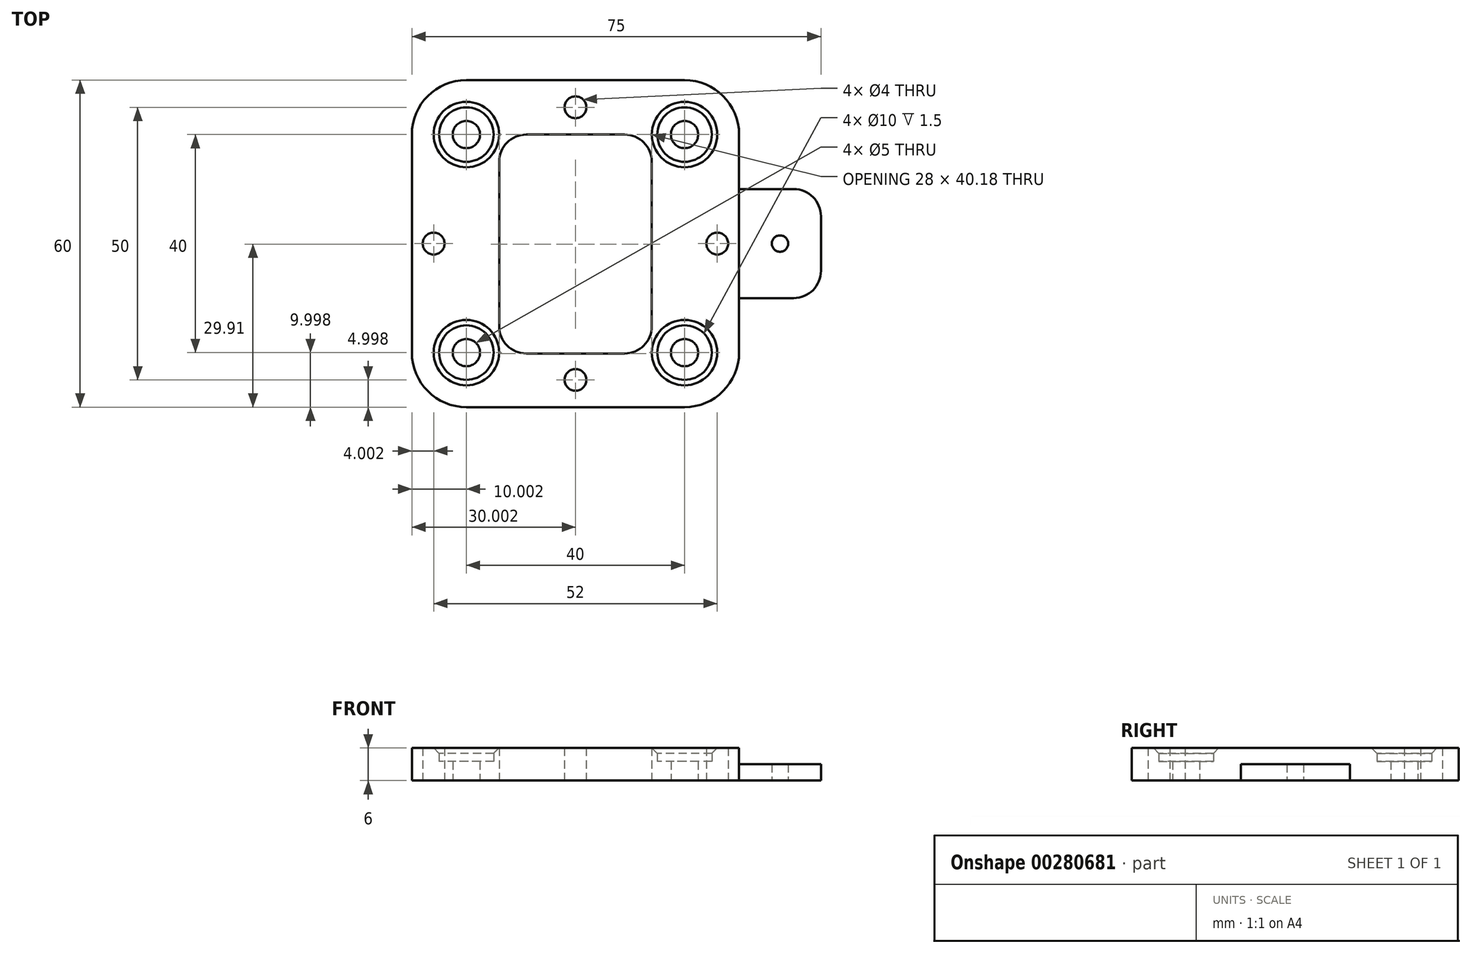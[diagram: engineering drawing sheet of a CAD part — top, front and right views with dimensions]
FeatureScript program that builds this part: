
annotation { "Feature Type Name" : "Feature", "Feature Type Description" : "" }
export const myFeature = defineFeature(function(context is Context, id is Id, definition is map)
    precondition{}
    {
        {
            var Q0;
            Q0=qCreatedBy(makeId("Top.planeOp"),FACE);
            var sketch = newSketch(context, id + "F0", { "sketchPlane" : qUnion([Q0])});
            skLineSegment(sketch, "E0.bottom", {"start": v(-88.55, 39.85) * mm, "end": v(-28.55, 39.85) * mm});
            skLineSegment(sketch, "E0.top", {"start": v(-88.55, -20.15) * mm, "end": v(-28.55, -20.15) * mm});
            skLineSegment(sketch, "E0.left", {"start": v(-88.55, 39.85) * mm, "end": v(-88.55, -20.15) * mm});
            skLineSegment(sketch, "E0.right", {"start": v(-28.55, 39.85) * mm, "end": v(-28.55, -20.15) * mm});
            skLineSegment(sketch, "E1.0", {"start": v(-78.55, 29.85) * mm, "end": v(-38.55, 29.85) * mm, "construction": true});
            skLineSegment(sketch, "E1.1", {"start": v(-78.55, 29.85) * mm, "end": v(-78.55, -10.15) * mm, "construction": true});
            skLineSegment(sketch, "E1.2", {"start": v(-78.55, -10.15) * mm, "end": v(-38.55, -10.15) * mm, "construction": true});
            skLineSegment(sketch, "E1.3", {"start": v(-38.55, 29.85) * mm, "end": v(-38.55, -10.15) * mm, "construction": true});
            skCircle(sketch, "E2", {"center": v(-78.55, 29.85) * mm, "radius": 5 * mm});
            skCircle(sketch, "E3", {"center": v(-78.55, -10.15) * mm, "radius": 5 * mm});
            skCircle(sketch, "E4", {"center": v(-38.55, 29.85) * mm, "radius": 5 * mm});
            skCircle(sketch, "E5", {"center": v(-38.55, -10.15) * mm, "radius": 5 * mm});
            skCircle(sketch, "E6", {"center": v(-78.55, 29.85) * mm, "radius": 2.5 * mm});
            skCircle(sketch, "E7", {"center": v(-38.55, 29.85) * mm, "radius": 2.5 * mm});
            skCircle(sketch, "E8", {"center": v(-38.55, -10.15) * mm, "radius": 2.5 * mm});
            skCircle(sketch, "E9", {"center": v(-78.55, -10.15) * mm, "radius": 2.5 * mm});
            skLineSegment(sketch, "E10.0", {"start": v(-72.55, 29.85) * mm, "end": v(-72.55, -10.33) * mm});
            skLineSegment(sketch, "E11.0", {"start": v(-44.55, 29.85) * mm, "end": v(-44.55, -10.33) * mm});
            skLineSegment(sketch, "E12", {"start": v(-72.55, 29.85) * mm, "end": v(-44.55, 29.85) * mm});
            skLineSegment(sketch, "E13", {"start": v(-44.55, -10.33) * mm, "end": v(-72.55, -10.33) * mm});
            skCircle(sketch, "E14", {"center": v(-84.55, 9.85) * mm, "radius": 2 * mm});
            skPoint(sketch, "E14.centerSnap0", {"position": v(-78.55, 9.85) * mm});
            skCircle(sketch, "E15", {"center": v(-32.55, 9.85) * mm, "radius": 2 * mm});
            skPoint(sketch, "E15.centerSnap0", {"position": v(-38.55, 9.85) * mm});
            skLineSegment(sketch, "E16.bottom", {"start": v(-28.55, 19.85) * mm, "end": v(-13.55, 19.85) * mm});
            skLineSegment(sketch, "E16.top", {"start": v(-28.55, -0.15) * mm, "end": v(-13.55, -0.15) * mm});
            skLineSegment(sketch, "E16.left", {"start": v(-28.55, 19.85) * mm, "end": v(-28.55, -0.15) * mm});
            skLineSegment(sketch, "E16.right", {"start": v(-13.55, 19.85) * mm, "end": v(-13.55, -0.15) * mm});
            skPoint(sketch, "E16.middle", {"position": v(-21.05, 9.85) * mm});
            skCircle(sketch, "E17", {"center": v(-21.05, 9.85) * mm, "radius": 1.5 * mm});
            skCircle(sketch, "E18", {"center": v(-58.55, 34.85) * mm, "radius": 2 * mm});
            skPoint(sketch, "E18.centerSnap0", {"position": v(-58.55, 29.85) * mm});
            skCircle(sketch, "E19", {"center": v(-58.55, -15.15) * mm, "radius": 2 * mm});
            skPoint(sketch, "E19.centerSnap0", {"position": v(-58.55, -10.33) * mm});
            skSolve(sketch);
        }
        {
            var Q0;
            Q0=makeQuery(id+"F0.imprint","IMPRINT",FACE,{"disambiguationData":[TD([[makeQuery(id+"F0.imprint","IMPRINT",EDGE,{"derivedFrom":sQuery(id+"F0.wireOp",EDGE,"E0.bottom")}),-1.0]])]});
            extrude(context, id + "F1", {"entities" : qUnion([Q0]), "depth" : 6 * mm, "offsetDistance" : 25 * mm});
        }
        {
            var Q0;
            Q0=makeQuery(id+"F0.imprint","IMPRINT",FACE,{"disambiguationData":[TD([[makeQuery(id+"F0.imprint","IMPRINT",EDGE,{"derivedFrom":sQuery(id+"F0.wireOp",EDGE,"E2")}),1.0]])]});
            var Q1;
            Q1=makeQuery(id+"F0.imprint","IMPRINT",FACE,{"disambiguationData":[TD([[makeQuery(id+"F0.imprint","IMPRINT",EDGE,{"derivedFrom":sQuery(id+"F0.wireOp",EDGE,"E3")}),1.0]])]});
            var Q2;
            Q2=makeQuery(id+"F0.imprint","IMPRINT",FACE,{"disambiguationData":[TD([[makeQuery(id+"F0.imprint","IMPRINT",EDGE,{"derivedFrom":sQuery(id+"F0.wireOp",EDGE,"E4")}),1.0]])]});
            var Q3;
            Q3=makeQuery(id+"F0.imprint","IMPRINT",FACE,{"disambiguationData":[TD([[makeQuery(id+"F0.imprint","IMPRINT",EDGE,{"derivedFrom":sQuery(id+"F0.wireOp",EDGE,"E5")}),1.0]])]});
            extrude(context, id + "F2", {"entities" : qUnion([Q0, Q1, Q2, Q3]), "operationType" : NewBodyOperationType.ADD, "depth" : 3.5 * mm, "offsetDistance" : 25 * mm});
        }
        {
            var Q0;
            Q0=makeQuery(id+"F0.imprint","IMPRINT",FACE,{"disambiguationData":[TD([[makeQuery(id+"F0.imprint","IMPRINT",EDGE,{"derivedFrom":sQuery(id+"F0.wireOp",EDGE,"E16.bottom")}),-1.0]])]});
            extrude(context, id + "F3", {"entities" : qUnion([Q0]), "operationType" : NewBodyOperationType.ADD, "depth" : 3 * mm, "offsetDistance" : 25 * mm});
        }
        {
            var Q0;
            Q0=makeQuery(id+"F1.opExtrude","SWEPT_EDGE",EDGE,{"disambiguationData":[OSD([sQuery(id+"F0.wireOp",EDGE,"E0.bottom"),sQuery(id+"F0.wireOp",EDGE,"E0.left")])]});
            var Q1;
            Q1=makeQuery(id+"F1.opExtrude","SWEPT_EDGE",EDGE,{"disambiguationData":[OSD([sQuery(id+"F0.wireOp",EDGE,"E0.top"),sQuery(id+"F0.wireOp",EDGE,"E0.left")])]});
            var Q2;
            Q2=makeQuery(id+"F1.opExtrude","SWEPT_EDGE",EDGE,{"disambiguationData":[OSD([sQuery(id+"F0.wireOp",EDGE,"E0.top"),sQuery(id+"F0.wireOp",EDGE,"E0.right")])]});
            var Q3;
            Q3=makeQuery(id+"F1.opExtrude","SWEPT_EDGE",EDGE,{"disambiguationData":[OSD([sQuery(id+"F0.wireOp",EDGE,"E0.bottom"),sQuery(id+"F0.wireOp",EDGE,"E0.right")])]});
            fillet(context, id + "F4", {"entities" : qUnion([Q0, Q1, Q2, Q3]), "radius" : 10 * mm, "tangentPropagation" : true, "allowEdgeOverflow" : false});
        }
        {
            var Q0;
            Q0=makeQuery(id+"F1.opExtrude","SWEPT_EDGE",EDGE,{"disambiguationData":[OSD([sQuery(id+"F0.wireOp",EDGE,"E11.0"),sQuery(id+"F0.wireOp",EDGE,"E12")])]});
            var Q1;
            Q1=makeQuery(id+"F1.opExtrude","SWEPT_EDGE",EDGE,{"disambiguationData":[OSD([sQuery(id+"F0.wireOp",EDGE,"E10.0"),sQuery(id+"F0.wireOp",EDGE,"E12")])]});
            var Q2;
            Q2=makeQuery(id+"F1.opExtrude","SWEPT_EDGE",EDGE,{"disambiguationData":[OSD([sQuery(id+"F0.wireOp",EDGE,"E10.0"),sQuery(id+"F0.wireOp",EDGE,"E13")])]});
            var Q3;
            Q3=makeQuery(id+"F1.opExtrude","SWEPT_EDGE",EDGE,{"disambiguationData":[OSD([sQuery(id+"F0.wireOp",EDGE,"E11.0"),sQuery(id+"F0.wireOp",EDGE,"E13")])]});
            var Q4;
            Q4=makeQuery(id+"F3.opExtrude","SWEPT_EDGE",EDGE,{"disambiguationData":[OSD([sQuery(id+"F0.wireOp",EDGE,"E0.right"),sQuery(id+"F0.wireOp",EDGE,"E16.top"),sQuery(id+"F0.wireOp",EDGE,"E16.left")])]});
            var Q5;
            Q5=makeQuery(id+"F3.opExtrude","SWEPT_EDGE",EDGE,{"disambiguationData":[OSD([sQuery(id+"F0.wireOp",EDGE,"E0.right"),sQuery(id+"F0.wireOp",EDGE,"E16.bottom"),sQuery(id+"F0.wireOp",EDGE,"E16.left")])]});
            var Q6;
            Q6=makeQuery(id+"F3.opExtrude","SWEPT_EDGE",EDGE,{"disambiguationData":[OSD([sQuery(id+"F0.wireOp",EDGE,"E16.top"),sQuery(id+"F0.wireOp",EDGE,"E16.right")])]});
            var Q7;
            Q7=makeQuery(id+"F3.opExtrude","SWEPT_EDGE",EDGE,{"disambiguationData":[OSD([sQuery(id+"F0.wireOp",EDGE,"E16.bottom"),sQuery(id+"F0.wireOp",EDGE,"E16.right")])]});
            fillet(context, id + "F5", {"entities" : qUnion([Q0, Q1, Q2, Q3, Q4, Q5, Q6, Q7]), "radius" : 5 * mm, "tangentPropagation" : true, "allowEdgeOverflow" : false});
        }
        {
            var Q0;
            Q0=makeQuery(id+"F1.opExtrude","CAP_EDGE",EDGE,{"disambiguationData":[OSD([sQuery(id+"F0.wireOp",EDGE,"E2")])],"isStart":false});
            var Q1;
            Q1=makeQuery(id+"F1.opExtrude","CAP_EDGE",EDGE,{"disambiguationData":[OSD([sQuery(id+"F0.wireOp",EDGE,"E3")])],"isStart":false});
            var Q2;
            Q2=makeQuery(id+"F1.opExtrude","CAP_EDGE",EDGE,{"disambiguationData":[OSD([sQuery(id+"F0.wireOp",EDGE,"E4")])],"isStart":false});
            var Q3;
            Q3=makeQuery(id+"F1.opExtrude","CAP_EDGE",EDGE,{"disambiguationData":[OSD([sQuery(id+"F0.wireOp",EDGE,"E5")])],"isStart":false});
            chamfer(context, id + "F6", {"entities" : qUnion([Q0, Q1, Q2, Q3]), "width" : 1 * mm, "tangentPropagation" : true});
        }
    });
